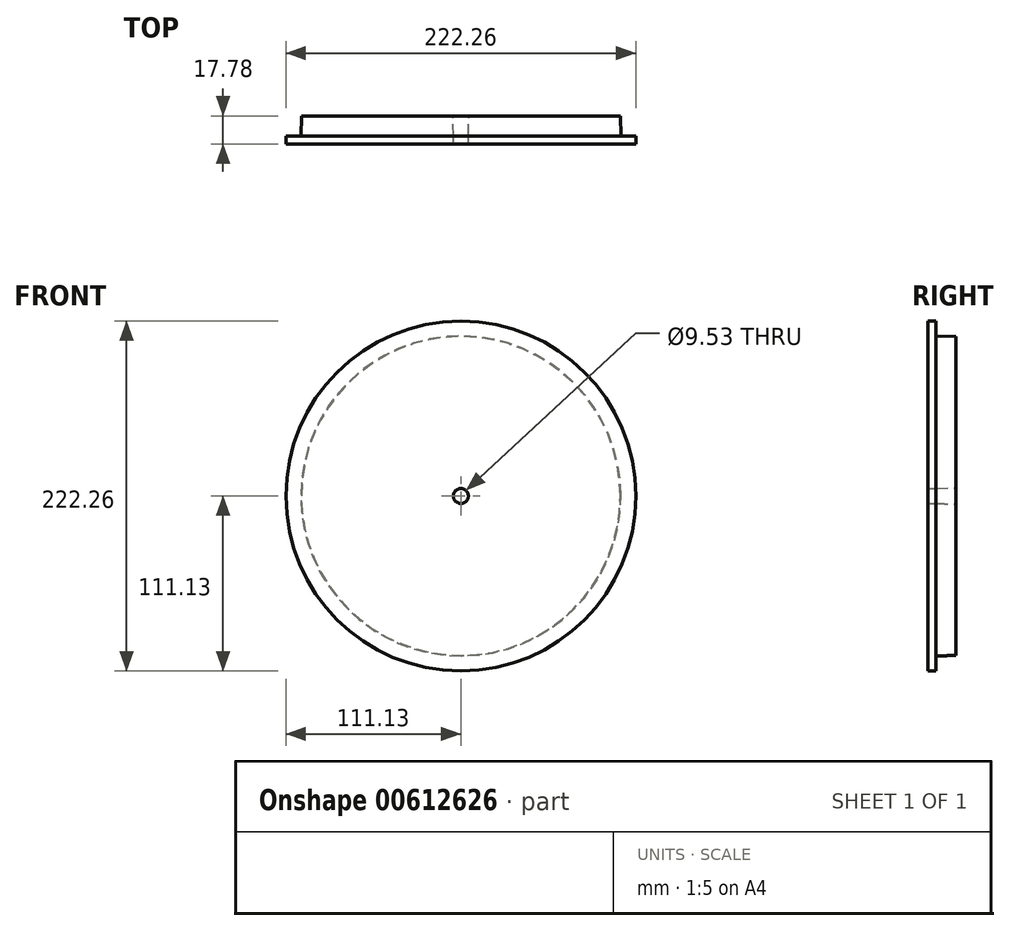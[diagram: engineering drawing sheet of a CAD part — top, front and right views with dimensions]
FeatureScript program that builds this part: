
annotation { "Feature Type Name" : "Feature", "Feature Type Description" : "" }
export const myFeature = defineFeature(function(context is Context, id is Id, definition is map)
    precondition{}
    {
        {
            var Q0;
            Q0=qCreatedBy(makeId("Front.planeOp"),FACE);
            var sketch = newSketch(context, id + "F0", { "sketchPlane" : qUnion([Q0])});
            skCircle(sketch, "E0", {"center": v(0, 0) * mm, "radius": 101.6 * mm});
            skCircle(sketch, "E1", {"center": v(0, 0) * mm, "radius": 111.13 * mm});
            skCircle(sketch, "E2", {"center": v(0, 0) * mm, "radius": 4.76 * mm});
            skSolve(sketch);
        }
        {
            var Q0;
            Q0=makeQuery(id+"F0.imprint","IMPRINT",FACE,{"disambiguationData":[TD([[makeQuery(id+"F0.imprint","IMPRINT",EDGE,{"derivedFrom":sQuery(id+"F0.wireOp",EDGE,"E0")}),1.0]])]});
            var Q1;
            Q1=sQuery(id+"F0.wireOp",EDGE,"E0");
            var Q2;
            Q2=sQuery(id+"F0.wireOp",EDGE,"E1");
            extrude(context, id + "F1", {"entities" : qUnion([Q0]), "surfaceEntities" : qUnion([Q1, Q2]), "oppositeDirection" : true, "depth" : 12.7 * mm, "offsetDistance" : 25.4 * mm, "hasDraft" : true, "draftAngle" : 1.5 * degree, "draftPullDirection" : true});
        }
        {
            var Q0;
            Q0 = qSketchRegion(id + "F0", true);
            var Q1;
            Q1=makeQuery(id+"F0.imprint","IMPRINT",FACE,{"disambiguationData":[TD([[makeQuery(id+"F0.imprint","IMPRINT",EDGE,{"derivedFrom":sQuery(id+"F0.wireOp",EDGE,"E0")}),1.0]])]});
            extrude(context, id + "F2", {"entities" : qUnion([Q0, Q1]), "operationType" : NewBodyOperationType.ADD, "depth" : 5.08 * mm, "offsetDistance" : 25.4 * mm});
        }
    });
